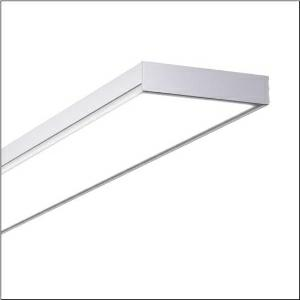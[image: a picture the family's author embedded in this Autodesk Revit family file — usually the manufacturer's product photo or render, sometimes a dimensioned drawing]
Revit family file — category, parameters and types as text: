
# Revit family: apollon_31_surface_51mp26wd2441ea
name_source: partatom
category: Lighting Fixtures
units: mm (PartAtom-declared; Revit-internal decimal feet)

## family parameters
Cut with Voids When Loaded = No
Host = Face
Light Source = No
Part Type = Normal
Room Calculation Point = No
Round Connector Dimension = Use Diameter
Shared = No

## types (1)
- Apollon 31 Surface (1 x LED, 4600 lm, 33 W, 4000K)
    Apparent Load = 33 VA
    CIE Flux Codes = 61 87 97 97 100
    Color Rendering = 80
    Color Temperature = 4000K
    Default Elevation = 1800 mm
    Description = Apollon 31 Surface, office luminaire, primary optical cover: micro prismatic cover, of PMMA, light emission: direct distribution, primary light characteristic: symmetric, installation type: surface-mounted, LED, rated luminous flux: 4.600lm, luminous efficacy: 139lm/W, light colour: 840, colour temperature: 4000K, control gear: DALI 2, with terminal, 5-pole, mains connection: 220..240V, AC, 50/60Hz, rated input power: 33W, housing, of sheet steel, coated, metallic grey (RAL 9006), length: 1.545mm, width: 200mm, height: 44mm, protection rating (complete): IP20, protection rating (on room side): IP40, protection rating (lamp compartment, on room side): IP40, insulation class (complete): insulation class I (protective earthing), certification: CE, ENEC, UKCA, impact resistance: IK02, permissible operating ambient temperature: -20..+40°C, standard: EN 60598-2-22, packaging unit: 1 piece
    Height = 44 mm
    Lamp = 1 x LED
    Lamp Light Flux = 4600 lm
    Lamp Power = 33 W
    Lamp count = 1
    Length = 1545 mm
    Luminous efficacy = 139 lm/W
    Manufacturer = Siteco
    ModVariant = No
    Model = 51MP26WD2441EA
    Mounting Place = Ceiling
    Mounting Type = Surface mounted
    Number of Poles = 1
    OnlyDefault = Yes
    Power Factor = 1
    Product Name = Apollon 31 Surface
    Product group = office luminaire | ceiling mounted
    ProductGroupID = 301
    Protection Class = Protection class I
    Protection Degree = IP 20
    RLX_Detail_Level = 1
    RLX_Emergency_Light_Flux = 0 lm
    RLX_Emergency_Type = 0
    RLX_Emergency_Type_DB = No
    RlxData = <blob elided: 24157 chars, md5=7c725021>
    Socket = socket
    Standby Power = 0 W
    System Light Flux = 4600 lm
    System Power = 33 W
    Type Comments = Product without accessories
    Type Image = l_1313654.jpg
    URL = http://relux.com
    VarID = ---
    Voltage = 0 V
    Weight = 0.00 kg
    Width = 200 mm  [stored 0.656168 ft]

note: [stored X ft] marks values corroborated as IEEE doubles in the binary element streams (Revit-internal decimal feet)

## geometry (parser evidence)
native form markers: Blend x4, Sweep x11
no freeform markers — native parametric forms only
